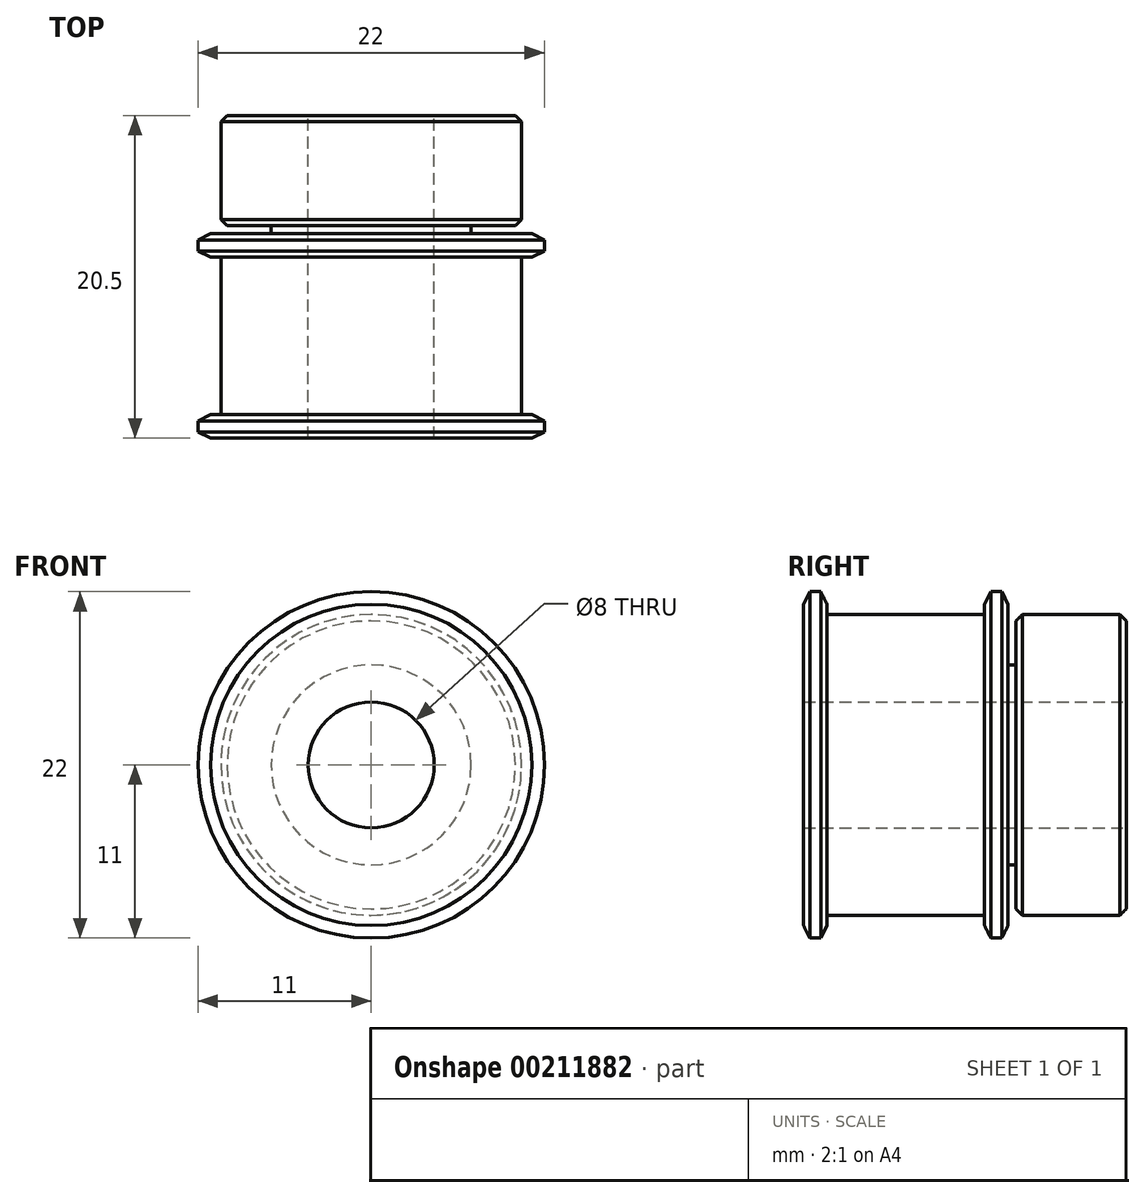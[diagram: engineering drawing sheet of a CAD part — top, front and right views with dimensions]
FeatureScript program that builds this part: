
annotation { "Feature Type Name" : "Feature", "Feature Type Description" : "" }
export const myFeature = defineFeature(function(context is Context, id is Id, definition is map)
    precondition{}
    {
        {
            var Q0;
            Q0=qCreatedBy(makeId("Right.planeOp"),FACE);
            var sketch = newSketch(context, id + "F0", { "sketchPlane" : qUnion([Q0])});
            skLineSegment(sketch, "E0", {"start": v(0, 0) * mm, "end": v(-6.32, 0) * mm, "construction": true});
            skLineSegment(sketch, "E1", {"start": v(-10.25, 4) * mm, "end": v(10.25, 4) * mm});
            skLineSegment(sketch, "E2", {"start": v(0, 4) * mm, "end": v(0, 0) * mm, "construction": true});
            skLineSegment(sketch, "E3", {"start": v(10.25, 9.55) * mm, "end": v(10.25, 11) * mm, "construction": true});
            skLineSegment(sketch, "E4", {"start": v(10.25, 11) * mm, "end": v(2.75, 11) * mm, "construction": true});
            skLineSegment(sketch, "E5", {"start": v(1.25, 11) * mm, "end": v(1.25, 9.55) * mm});
            skLineSegment(sketch, "E6", {"start": v(1.25, 9.55) * mm, "end": v(-8.75, 9.55) * mm});
            skLineSegment(sketch, "E7", {"start": v(-8.75, 9.55) * mm, "end": v(-8.75, 11) * mm});
            skLineSegment(sketch, "E8", {"start": v(-8.75, 11) * mm, "end": v(-10.25, 11) * mm});
            skLineSegment(sketch, "E9", {"start": v(-10.25, 11) * mm, "end": v(-10.25, 4) * mm});
            skLineSegment(sketch, "E10", {"start": v(2.75, 11) * mm, "end": v(2.75, 6.35) * mm});
            skLineSegment(sketch, "E11", {"start": v(2.75, 6.35) * mm, "end": v(3.25, 6.35) * mm});
            skLineSegment(sketch, "E12", {"start": v(2.75, 11) * mm, "end": v(1.25, 11) * mm});
            skLineSegment(sketch, "E13", {"start": v(3.25, 6.35) * mm, "end": v(3.25, 9.55) * mm});
            skLineSegment(sketch, "E14", {"start": v(3.25, 9.55) * mm, "end": v(10.25, 9.55) * mm});
            skLineSegment(sketch, "E15", {"start": v(10.25, 9.55) * mm, "end": v(10.25, 4) * mm});
            skSolve(sketch);
        }
        {
            var Q0;
            Q0=qSketchRegion(id+"F0",true);
            var Q1;
            Q1=sQuery(id+"F0.wireOp",EDGE,"E0");
            revolve(context, id + "F1", {"entities" : qUnion([Q0]), "axis" : qUnion([Q1]), "revolveType" : RevolveType.FULL});
        }
        {
            var Q0;
            Q0=makeQuery(id+"F1.opRevolve","SWEPT_EDGE",EDGE,{"disambiguationData":[OSD([sQuery(id+"F0.wireOp",EDGE,"E5"),sQuery(id+"F0.wireOp",EDGE,"E12")])]});
            var Q1;
            Q1=makeQuery(id+"F1.opRevolve","SWEPT_EDGE",EDGE,{"disambiguationData":[OSD([sQuery(id+"F0.wireOp",EDGE,"E10"),sQuery(id+"F0.wireOp",EDGE,"E12")])]});
            var Q2;
            Q2=makeQuery(id+"F1.opRevolve","SWEPT_EDGE",EDGE,{"disambiguationData":[OSD([sQuery(id+"F0.wireOp",EDGE,"E8"),sQuery(id+"F0.wireOp",EDGE,"E9")])]});
            chamfer(context, id + "F2", {"entities" : qUnion([Q0, Q1, Q2]), "chamferType" : ChamferType.TWO_OFFSETS, "width1" : .4 * mm, "oppositeDirection" : false, "width2" : .8 * mm, "tangentPropagation" : true});
        }
        {
            var Q0;
            Q0=makeQuery(id+"F1.opRevolve","SWEPT_EDGE",EDGE,{"disambiguationData":[OSD([sQuery(id+"F0.wireOp",EDGE,"E7"),sQuery(id+"F0.wireOp",EDGE,"E8")])]});
            chamfer(context, id + "F3", {"entities" : qUnion([Q0]), "chamferType" : ChamferType.TWO_OFFSETS, "width1" : .8 * mm, "oppositeDirection" : false, "width2" : .4 * mm, "tangentPropagation" : true});
        }
        {
            var Q0;
            Q0=makeQuery(id+"F1.opRevolve","SWEPT_EDGE",EDGE,{"disambiguationData":[OSD([sQuery(id+"F0.wireOp",EDGE,"E13"),sQuery(id+"F0.wireOp",EDGE,"E14")])]});
            var Q1;
            Q1=makeQuery(id+"F1.opRevolve","SWEPT_EDGE",EDGE,{"disambiguationData":[OSD([sQuery(id+"F0.wireOp",EDGE,"E14"),sQuery(id+"F0.wireOp",EDGE,"E15")])]});
            chamfer(context, id + "F4", {"entities" : qUnion([Q0, Q1]), "width" : .4 * mm, "tangentPropagation" : true});
        }
    });
